# Revit family: L. Estudio Angular
name_source: partatom
category: Plumbing Fixtures
revit_build: Autodesk Revit 2015 (Build: 20140322_1515(x64)
units: mm (PartAtom-declared; Revit-internal decimal feet)

## types (1)
- L. Estudio Angular
    Assembly Code = D2010.60
    BIMobject category = Basins
    BT_Color = Cromo
    BT_Itemizado_Estandar_CDT = H 06 06 00
    BT_Material = Cromo
    BT_SKU = 00 00 00
    BT_Uso = Sanitario
    Corner washbasin = Yes
    Depth = 518 mm
    Description = L. Estudio Angular
    Drain Diameter = 46 mm
    Edition number = 1
    Height = 367 mm
    ID_Objeto = BT_F_F_1770
    ID_Source = BIMTOOL
    IFC Classification = Sanitary Terminal
    Imported Category Visibility 01 = Yes
    Imported Category Visibility 02 = No
    Installation type = Wall-hung
    Keynote = 22 31 13
    Length = 605 mm
    Manufacturer = Roca
    Manufacturer name = Roca
    Material = Vitreous china
    Material main = Vitreous china
    Model = L. Estudio Angular
    NBS Reference Code = 35-65-70-94
    NBS Reference Description = Wash Basin Systems
    Nominal height = 200
    Nominal width = 605
    Primary Material = White - Estudio Angular - Roca
    Product SKU = 325200001
    Product family = Estudio Angular
    Product group = BASINS
    Secondary Material = Cromo
    Shape = Corner
    Supplier = Mk
    Taphole Diameter = 35 mm
    Taphole configuration = 1 Taphole in the middle
    Type Comments = L. Estudio Angular
    URL = http://www.export.roca.com
    Uniclass 1.4 Code = L7212
    Uniclass 1.4 Description = Washbasins
    Uniclass 2.0 Code = SS-35-65-70-94
    Uniclass 2.0 Description = Wash Basin Systems
    Weight Net (Kg) = 0
    Width = 519 mm

## geometry (parser evidence)
native form markers: Blend x6, Extrusion x3, Sweep x5
no freeform markers — native parametric forms only
